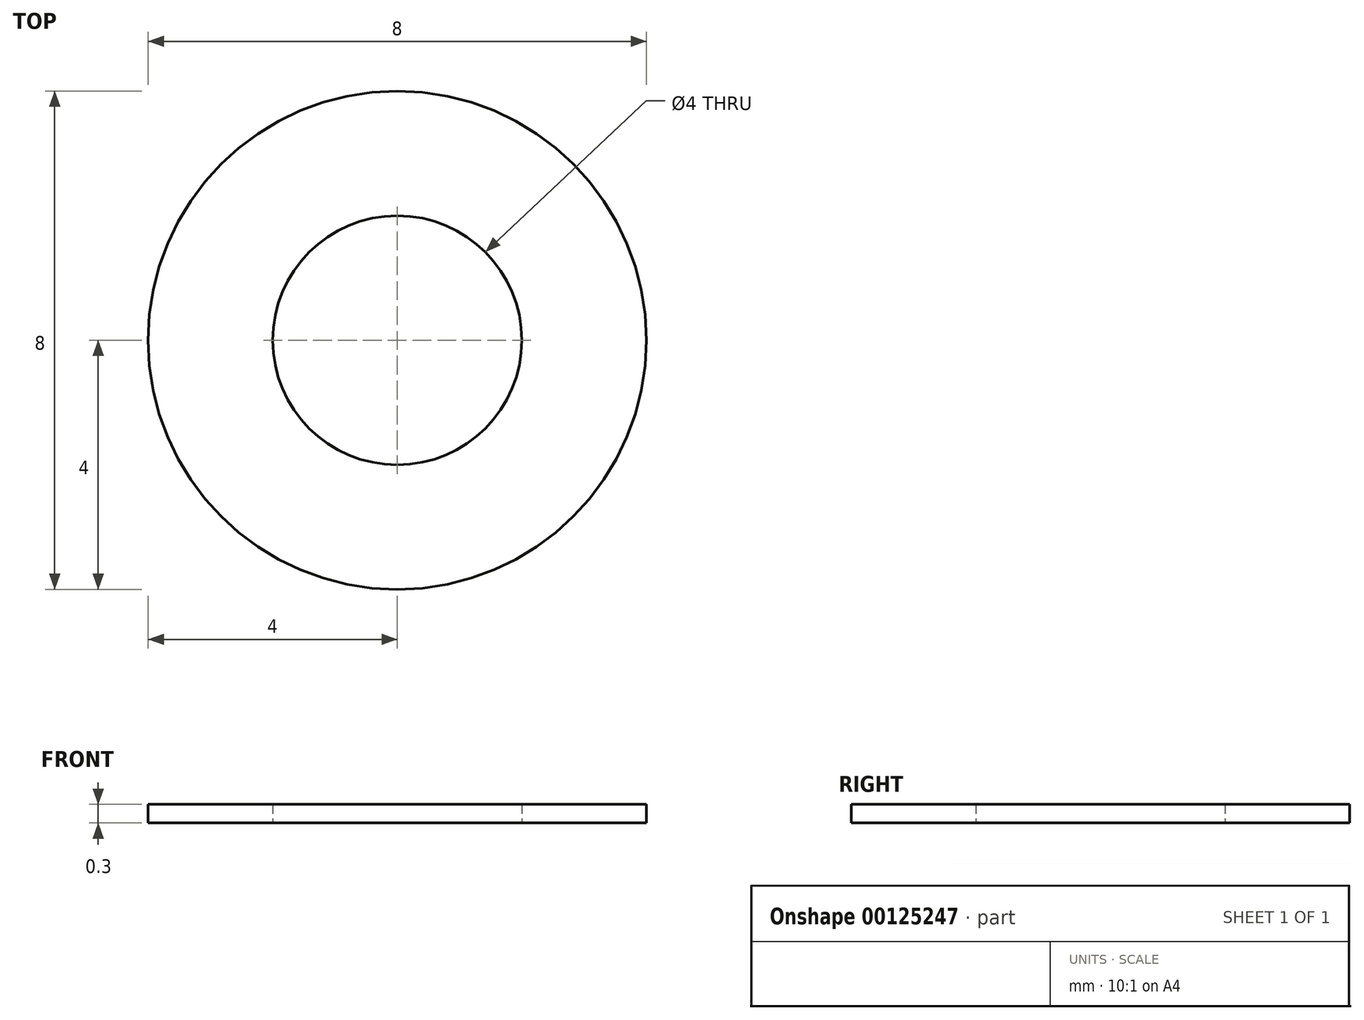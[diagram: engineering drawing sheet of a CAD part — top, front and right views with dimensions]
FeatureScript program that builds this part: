
annotation { "Feature Type Name" : "Feature", "Feature Type Description" : "" }
export const myFeature = defineFeature(function(context is Context, id is Id, definition is map)
    precondition{}
    {
        {
            var Q0;
            Q0=qCreatedBy(makeId("Top.planeOp"),FACE);
            var sketch = newSketch(context, id + "F0", { "sketchPlane" : qUnion([Q0])});
            skCircle(sketch, "E0", {"center": v(0, 0) * mm, "radius": 4 * mm});
            skCircle(sketch, "E1", {"center": v(0, 0) * mm, "radius": 2 * mm});
            skSolve(sketch);
        }
        {
            var Q0;
            Q0=makeQuery(id+"F0.imprint","IMPRINT",FACE,{"disambiguationData":[TD([[makeQuery(id+"F0.imprint","IMPRINT",EDGE,{"derivedFrom":sQuery(id+"F0.wireOp",EDGE,"E0")}),1.0]])]});
            extrude(context, id + "F1", {"entities" : qUnion([Q0]), "depth" : .3 * mm});
        }
    });
